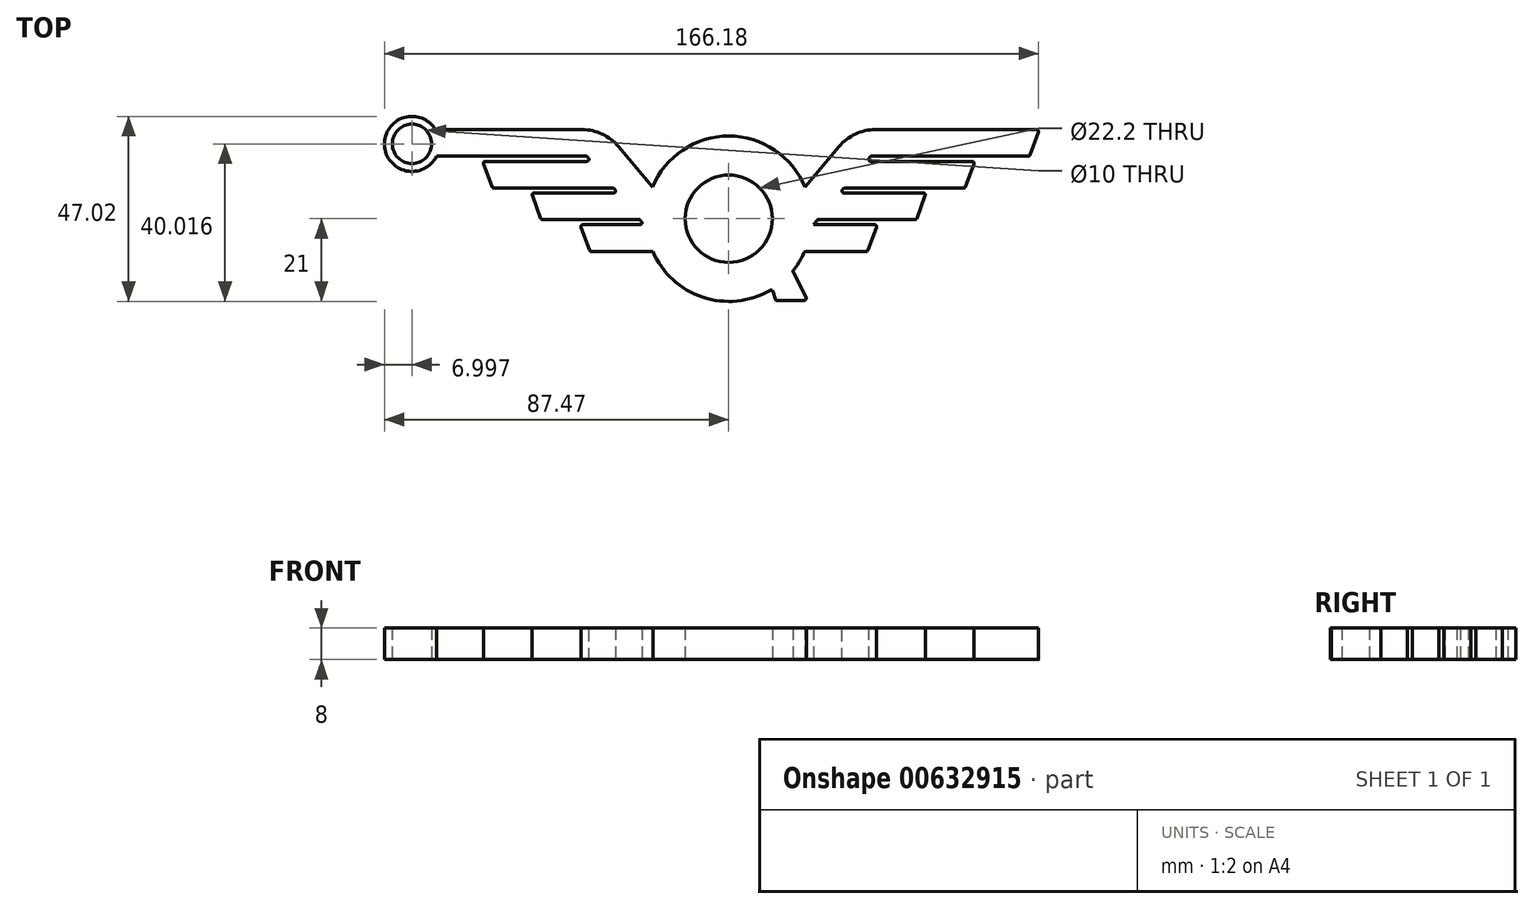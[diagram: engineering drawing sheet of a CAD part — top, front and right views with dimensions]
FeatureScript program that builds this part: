
annotation { "Feature Type Name" : "Feature", "Feature Type Description" : "" }
export const myFeature = defineFeature(function(context is Context, id is Id, definition is map)
    precondition{}
    {
        {
            var Q0;
            Q0=qCreatedBy(makeId("Top.planeOp"),FACE);
            var sketch = newSketch(context, id + "F0", { "sketchPlane" : qUnion([Q0])});
            skCircle(sketch, "E0", {"center": v(0, 0) * mm, "radius": 21 * mm});
            skLineSegment(sketch, "E1", {"start": v(11, -17.89) * mm, "end": v(12, -20.84) * mm});
            skLineSegment(sketch, "E2", {"start": v(12, -20.84) * mm, "end": v(20, -20.74) * mm});
            skLineSegment(sketch, "E3", {"start": v(20, -20.74) * mm, "end": v(16.26, -13.29) * mm});
            skCircle(sketch, "E4.0", {"center": v(0, 0) * mm, "radius": 11.1 * mm});
            skLineSegment(sketch, "E5", {"start": v(37.76, -1.52) * mm, "end": v(20.94, -1.52) * mm});
            skLineSegment(sketch, "E6", {"start": v(35.3, -8.29) * mm, "end": v(19.3, -8.29) * mm});
            skLineSegment(sketch, "E7", {"start": v(37.76, -1.52) * mm, "end": v(35.3, -8.29) * mm});
            skLineSegment(sketch, "E8.MirrorCS", {"start": v(-37.76, -1.52) * mm, "end": v(-20.94, -1.52) * mm});
            skLineSegment(sketch, "E9.MirrorCS", {"start": v(-35.3, -8.29) * mm, "end": v(-19.3, -8.29) * mm});
            skLineSegment(sketch, "E10.MirrorCS", {"start": v(-37.76, -1.52) * mm, "end": v(-35.3, -8.29) * mm});
            skLineSegment(sketch, "E11", {"start": v(31.64, 22.63) * mm, "end": v(78.92, 22.63) * mm});
            skLineSegment(sketch, "E12", {"start": v(54.5, 15.87) * mm, "end": v(62.74, 15.87) * mm});
            skLineSegment(sketch, "E13", {"start": v(78.92, 22.63) * mm, "end": v(76.46, 15.87) * mm});
            skLineSegment(sketch, "E14", {"start": v(76.46, 15.87) * mm, "end": v(62.74, 15.87) * mm});
            skLineSegment(sketch, "E15", {"start": v(54.5, 15.87) * mm, "end": v(36.02, 15.87) * mm});
            skLineSegment(sketch, "E16", {"start": v(47.43, 7.82) * mm, "end": v(60.05, 7.82) * mm});
            skLineSegment(sketch, "E17", {"start": v(62.52, 14.59) * mm, "end": v(60.05, 7.82) * mm});
            skLineSegment(sketch, "E18", {"start": v(29.64, 6.54) * mm, "end": v(50.14, 6.54) * mm});
            skLineSegment(sketch, "E19", {"start": v(23, -0.22) * mm, "end": v(47.67, -0.22) * mm});
            skLineSegment(sketch, "E20", {"start": v(50.14, 6.54) * mm, "end": v(47.67, -0.22) * mm});
            skLineSegment(sketch, "E21", {"start": v(34.95, 14.59) * mm, "end": v(43.97, 14.59) * mm});
            skLineSegment(sketch, "E22", {"start": v(47.43, 7.82) * mm, "end": v(29.29, 7.82) * mm});
            skLineSegment(sketch, "E23", {"start": v(47.67, -0.22) * mm, "end": v(22.55, -0.22) * mm});
            skLineSegment(sketch, "E24", {"start": v(22.55, -0.22) * mm, "end": v(21.47, -1.52) * mm});
            skLineSegment(sketch, "E25", {"start": v(62.52, 14.59) * mm, "end": v(34.95, 14.59) * mm});
            skLineSegment(sketch, "E26", {"start": v(36.02, 15.87) * mm, "end": v(34.95, 14.59) * mm});
            skLineSegment(sketch, "E27", {"start": v(43.97, 14.59) * mm, "end": v(34.95, 14.59) * mm});
            skLineSegment(sketch, "E28", {"start": v(29.64, 6.54) * mm, "end": v(28.21, 6.54) * mm});
            skLineSegment(sketch, "E29", {"start": v(29.29, 7.82) * mm, "end": v(28.21, 6.54) * mm});
            skLineSegment(sketch, "E30", {"start": v(31.64, 22.63) * mm, "end": v(19.4, 8.02) * mm});
            skLineSegment(sketch, "E31.MirrorCS", {"start": v(-31.64, 22.63) * mm, "end": v(-19.4, 8.02) * mm});
            skLineSegment(sketch, "E32.MirrorCS", {"start": v(-31.64, 22.63) * mm, "end": v(-78.92, 22.63) * mm});
            skLineSegment(sketch, "E33.MirrorCS", {"start": v(-54.5, 15.87) * mm, "end": v(-36.02, 15.87) * mm});
            skLineSegment(sketch, "E34.MirrorCS", {"start": v(-34.95, 14.59) * mm, "end": v(-43.97, 14.59) * mm});
            skLineSegment(sketch, "E35.MirrorCS", {"start": v(-36.02, 15.87) * mm, "end": v(-34.95, 14.59) * mm});
            skLineSegment(sketch, "E36.MirrorCS", {"start": v(-54.5, 15.87) * mm, "end": v(-62.74, 15.87) * mm});
            skLineSegment(sketch, "E37.MirrorCS", {"start": v(-76.46, 15.87) * mm, "end": v(-62.74, 15.87) * mm});
            skLineSegment(sketch, "E38.MirrorCS", {"start": v(-78.92, 22.63) * mm, "end": v(-76.46, 15.87) * mm});
            skLineSegment(sketch, "E39.MirrorCS", {"start": v(-62.52, 14.59) * mm, "end": v(-34.95, 14.59) * mm});
            skLineSegment(sketch, "E40.MirrorCS", {"start": v(-62.52, 14.59) * mm, "end": v(-60.05, 7.82) * mm});
            skLineSegment(sketch, "E41.MirrorCS", {"start": v(-47.43, 7.82) * mm, "end": v(-60.05, 7.82) * mm});
            skLineSegment(sketch, "E42.MirrorCS", {"start": v(-47.43, 7.82) * mm, "end": v(-29.29, 7.82) * mm});
            skLineSegment(sketch, "E43.MirrorCS", {"start": v(-29.29, 7.82) * mm, "end": v(-28.21, 6.54) * mm});
            skLineSegment(sketch, "E44.MirrorCS", {"start": v(-29.64, 6.54) * mm, "end": v(-28.21, 6.54) * mm});
            skLineSegment(sketch, "E45.MirrorCS", {"start": v(-29.64, 6.54) * mm, "end": v(-50.14, 6.54) * mm});
            skLineSegment(sketch, "E46.MirrorCS", {"start": v(-50.14, 6.54) * mm, "end": v(-47.67, -0.22) * mm});
            skLineSegment(sketch, "E47.MirrorCS", {"start": v(-47.67, -0.22) * mm, "end": v(-22.55, -0.22) * mm});
            skLineSegment(sketch, "E48.MirrorCS", {"start": v(-22.55, -0.22) * mm, "end": v(-21.47, -1.52) * mm});
            skSolve(sketch);
        }
        {
            var Q0;
            Q0=makeQuery(id+"F0.imprint","IMPRINT",FACE,{"disambiguationData":[TD([[makeQuery(id+"F0.imprint","IMPRINT",EDGE,{"derivedFrom":sQuery(id+"F0.wireOp",EDGE,"E4.0")}),-1.0]])]});
            var Q1;
            {var subQ0=sQuery(id+"F0.wireOp",EDGE,"E1");Q1=makeQuery(id+"F0.imprint","IMPRINT",FACE,{"disambiguationData":[TD([[makeQuery(id+"F0.imprint","IMPRINT",EDGE,{"derivedFrom":subQ0}),1.0]])]});}
            extrude(context, id + "F1", {"entities" : qUnion([Q0, Q1]), "endBound" : BoundingType.SYMMETRIC, "depth" : 8 * mm, "offsetDistance" : 25 * mm});
        }
        {
            var Q0;
            {var subQ3=sQuery(id+"F0.wireOp",EDGE,"dh19a1xa-YlTx-h9a7-XIYp-d6YBFNoYxual");Q0=makeQuery(id+"F0.imprint","IMPRINT",FACE,{"disambiguationData":[TD([[makeQuery(id+"F0.imprint","IMPRINT",EDGE,{"derivedFrom":subQ3}),-1.0]])]});}
            var Q1;
            {var subQ0=sQuery(id+"F0.wireOp",EDGE,"E6");Q1=makeQuery(id+"F0.imprint","IMPRINT",FACE,{"disambiguationData":[TD([[makeQuery(id+"F0.imprint","IMPRINT",EDGE,{"derivedFrom":subQ0}),-1.0]])]});}
            extrude(context, id + "F2", {"entities" : qUnion([Q0, Q1]), "operationType" : NewBodyOperationType.ADD, "endBound" : BoundingType.SYMMETRIC, "depth" : 8 * mm, "offsetDistance" : 25 * mm});
        }
        {
            var Q0;
            Q0=makeQuery(id+"F0.imprint","IMPRINT",FACE,{"disambiguationData":[TD([[makeQuery(id+"F0.imprint","IMPRINT",EDGE,{"derivedFrom":sQuery(id+"F0.wireOp",EDGE,"E11")}),-1.0]])]});
            extrude(context, id + "F3", {"entities" : qUnion([Q0]), "operationType" : NewBodyOperationType.ADD, "endBound" : BoundingType.SYMMETRIC, "depth" : 8 * mm, "offsetDistance" : 25 * mm});
        }
        {
            var Q0;
            Q0 = qSketchRegion(id + "F0", true);
            extrude(context, id + "F4", {"entities" : qUnion([Q0]), "operationType" : NewBodyOperationType.ADD, "endBound" : BoundingType.SYMMETRIC, "depth" : 8 * mm, "offsetDistance" : 25 * mm});
        }
        {
            var Q0;
            Q0=makeQuery(id+"F4.opExtrude","SWEPT_EDGE",EDGE,{"disambiguationData":[OSD([sQuery(id+"F0.wireOp",EDGE,"E33.MirrorCS"),sQuery(id+"F0.wireOp",EDGE,"E35.MirrorCS")])]});
            var Q1;
            Q1=makeQuery(id+"F4.opExtrude","SWEPT_EDGE",EDGE,{"disambiguationData":[OSD([sQuery(id+"F0.wireOp",EDGE,"E42.MirrorCS"),sQuery(id+"F0.wireOp",EDGE,"E43.MirrorCS")])]});
            var Q2;
            Q2=makeQuery(id+"F4.opExtrude","SWEPT_EDGE",EDGE,{"disambiguationData":[OSD([sQuery(id+"F0.wireOp",EDGE,"E48.MirrorCS"),sQuery(id+"F0.wireOp",EDGE,"E47.MirrorCS")])]});
            var Q3;
            Q3=makeQuery(id+"F4.opExtrude","SWEPT_EDGE",EDGE,{"disambiguationData":[OSD([sQuery(id+"F0.wireOp",EDGE,"E0"),sQuery(id+"F0.wireOp",EDGE,"E9.MirrorCS")])]});
            var Q4;
            Q4=makeQuery(id+"F4.opExtrude","SWEPT_EDGE",EDGE,{"disambiguationData":[OSD([sQuery(id+"F0.wireOp",EDGE,"E8.MirrorCS"),sQuery(id+"F0.wireOp",EDGE,"E48.MirrorCS")])]});
            var Q5;
            Q5=makeQuery(id+"F4.opExtrude","SWEPT_EDGE",EDGE,{"disambiguationData":[OSD([sQuery(id+"F0.wireOp",EDGE,"E43.MirrorCS"),sQuery(id+"F0.wireOp",EDGE,"E44.MirrorCS")])]});
            var Q6;
            Q6=makeQuery(id+"F4.opExtrude","SWEPT_EDGE",EDGE,{"disambiguationData":[OSD([sQuery(id+"F0.wireOp",EDGE,"E35.MirrorCS"),sQuery(id+"F0.wireOp",EDGE,"E39.MirrorCS")])]});
            var Q7;
            Q7=makeQuery(id+"F4.opExtrude","SWEPT_EDGE",EDGE,{"disambiguationData":[OSD([sQuery(id+"F0.wireOp",EDGE,"E32.MirrorCS"),sQuery(id+"F0.wireOp",EDGE,"E38.MirrorCS")])]});
            var Q8;
            Q8=makeQuery(id+"F4.opExtrude","SWEPT_EDGE",EDGE,{"disambiguationData":[OSD([sQuery(id+"F0.wireOp",EDGE,"E37.MirrorCS"),sQuery(id+"F0.wireOp",EDGE,"E38.MirrorCS")])]});
            var Q9;
            Q9=makeQuery(id+"F4.opExtrude","SWEPT_EDGE",EDGE,{"disambiguationData":[OSD([sQuery(id+"F0.wireOp",EDGE,"E39.MirrorCS"),sQuery(id+"F0.wireOp",EDGE,"E40.MirrorCS")])]});
            var Q10;
            Q10=makeQuery(id+"F4.opExtrude","SWEPT_EDGE",EDGE,{"disambiguationData":[OSD([sQuery(id+"F0.wireOp",EDGE,"E40.MirrorCS"),sQuery(id+"F0.wireOp",EDGE,"E41.MirrorCS")])]});
            var Q11;
            Q11=makeQuery(id+"F4.opExtrude","SWEPT_EDGE",EDGE,{"disambiguationData":[OSD([sQuery(id+"F0.wireOp",EDGE,"E45.MirrorCS"),sQuery(id+"F0.wireOp",EDGE,"E46.MirrorCS")])]});
            var Q12;
            Q12=makeQuery(id+"F4.opExtrude","SWEPT_EDGE",EDGE,{"disambiguationData":[OSD([sQuery(id+"F0.wireOp",EDGE,"E8.MirrorCS"),sQuery(id+"F0.wireOp",EDGE,"E10.MirrorCS")])]});
            var Q13;
            Q13=makeQuery(id+"F4.opExtrude","SWEPT_EDGE",EDGE,{"disambiguationData":[OSD([sQuery(id+"F0.wireOp",EDGE,"E9.MirrorCS"),sQuery(id+"F0.wireOp",EDGE,"E10.MirrorCS")])]});
            var Q14;
            Q14=makeQuery(id+"F4.opExtrude","SWEPT_EDGE",EDGE,{"disambiguationData":[OSD([sQuery(id+"F0.wireOp",EDGE,"E46.MirrorCS"),sQuery(id+"F0.wireOp",EDGE,"E47.MirrorCS")])]});
            var Q15;
            Q15=makeQuery(id+"F3.opExtrude","SWEPT_EDGE",EDGE,{"disambiguationData":[OSD([sQuery(id+"F0.wireOp",EDGE,"E11"),sQuery(id+"F0.wireOp",EDGE,"E13")])]});
            var Q16;
            Q16=makeQuery(id+"F3.opExtrude","SWEPT_EDGE",EDGE,{"disambiguationData":[OSD([sQuery(id+"F0.wireOp",EDGE,"E13"),sQuery(id+"F0.wireOp",EDGE,"E14")])]});
            var Q17;
            Q17=makeQuery(id+"F3.opExtrude","SWEPT_EDGE",EDGE,{"disambiguationData":[OSD([sQuery(id+"F0.wireOp",EDGE,"E17"),sQuery(id+"F0.wireOp",EDGE,"E25")])]});
            var Q18;
            Q18=makeQuery(id+"F3.opExtrude","SWEPT_EDGE",EDGE,{"disambiguationData":[OSD([sQuery(id+"F0.wireOp",EDGE,"E16"),sQuery(id+"F0.wireOp",EDGE,"E17")])]});
            var Q19;
            Q19=makeQuery(id+"F3.opExtrude","SWEPT_EDGE",EDGE,{"disambiguationData":[OSD([sQuery(id+"F0.wireOp",EDGE,"E18"),sQuery(id+"F0.wireOp",EDGE,"E20")])]});
            var Q20;
            Q20=makeQuery(id+"F2.opExtrude","SWEPT_EDGE",EDGE,{"disambiguationData":[OSD([sQuery(id+"F0.wireOp",EDGE,"E5"),sQuery(id+"F0.wireOp",EDGE,"E7")])]});
            var Q21;
            Q21=makeQuery(id+"F2.opExtrude","SWEPT_EDGE",EDGE,{"disambiguationData":[OSD([sQuery(id+"F0.wireOp",EDGE,"E6"),sQuery(id+"F0.wireOp",EDGE,"E7")])]});
            var Q22;
            Q22=makeQuery(id+"F3.opExtrude","SWEPT_EDGE",EDGE,{"disambiguationData":[OSD([sQuery(id+"F0.wireOp",EDGE,"E20"),sQuery(id+"F0.wireOp",EDGE,"E23")])]});
            var Q23;
            Q23=makeQuery(id+"F3.opExtrude","SWEPT_EDGE",EDGE,{"disambiguationData":[OSD([sQuery(id+"F0.wireOp",EDGE,"E5"),sQuery(id+"F0.wireOp",EDGE,"E24")])]});
            var Q24;
            Q24=makeQuery(id+"F3.opExtrude","SWEPT_EDGE",EDGE,{"disambiguationData":[OSD([sQuery(id+"F0.wireOp",EDGE,"E28"),sQuery(id+"F0.wireOp",EDGE,"E29")])]});
            var Q25;
            Q25=makeQuery(id+"F3.opExtrude","SWEPT_EDGE",EDGE,{"disambiguationData":[OSD([sQuery(id+"F0.wireOp",EDGE,"E26"),sQuery(id+"F0.wireOp",EDGE,"E27")])]});
            var Q26;
            Q26=makeQuery(id+"F3.opExtrude","SWEPT_EDGE",EDGE,{"disambiguationData":[OSD([sQuery(id+"F0.wireOp",EDGE,"E15"),sQuery(id+"F0.wireOp",EDGE,"E26")])]});
            var Q27;
            Q27=makeQuery(id+"F3.opExtrude","SWEPT_EDGE",EDGE,{"disambiguationData":[OSD([sQuery(id+"F0.wireOp",EDGE,"E22"),sQuery(id+"F0.wireOp",EDGE,"E29")])]});
            var Q28;
            Q28=makeQuery(id+"F3.opExtrude","SWEPT_EDGE",EDGE,{"disambiguationData":[OSD([sQuery(id+"F0.wireOp",EDGE,"E23"),sQuery(id+"F0.wireOp",EDGE,"E24")])]});
            var Q29;
            Q29=makeQuery(id+"F2.opExtrude","SWEPT_EDGE",EDGE,{"disambiguationData":[OSD([sQuery(id+"F0.wireOp",EDGE,"E0"),sQuery(id+"F0.wireOp",EDGE,"E6")])]});
            var Q30;
            Q30=makeQuery(id+"F1.opExtrude","SWEPT_EDGE",EDGE,{"disambiguationData":[OSD([sQuery(id+"F0.wireOp",EDGE,"E2"),sQuery(id+"F0.wireOp",EDGE,"E3")])]});
            var Q31;
            Q31=makeQuery(id+"F1.opExtrude","SWEPT_EDGE",EDGE,{"disambiguationData":[OSD([sQuery(id+"F0.wireOp",EDGE,"E1"),sQuery(id+"F0.wireOp",EDGE,"E2")])]});
            var Q32;
            Q32=makeQuery(id+"F1.opExtrude","SWEPT_EDGE",EDGE,{"disambiguationData":[OSD([sQuery(id+"F0.wireOp",EDGE,"E0"),sQuery(id+"F0.wireOp",EDGE,"E1")])]});
            var Q33;
            Q33=makeQuery(id+"F1.opExtrude","SWEPT_EDGE",EDGE,{"disambiguationData":[OSD([sQuery(id+"F0.wireOp",EDGE,"E0"),sQuery(id+"F0.wireOp",EDGE,"E3")])]});
            fillet(context, id + "F5", {"entities" : qUnion([Q0, Q1, Q2, Q3, Q4, Q5, Q6, Q7, Q8, Q9, Q10, Q11, Q12, Q13, Q14, Q15, Q16, Q17, Q18, Q19, Q20, Q21, Q22, Q23, Q24, Q25, Q26, Q27, Q28, Q29, Q30, Q31, Q32, Q33]), "radius" : .5 * mm, "tangentPropagation" : true, "allowEdgeOverflow" : false});
        }
        {
            var Q0;
            Q0=qCreatedBy(makeId("Top.planeOp"),FACE);
            var sketch = newSketch(context, id + "F6", { "sketchPlane" : qUnion([Q0])});
            skCircle(sketch, "E49", {"center": v(-80.47, 19.02) * mm, "radius": 7 * mm});
            skCircle(sketch, "E50.0", {"center": v(-80.47, 19.02) * mm, "radius": 5 * mm});
            skSolve(sketch);
        }
        {
            var Q0;
            Q0 = qSketchRegion(id + "F6", true);
            extrude(context, id + "F7", {"entities" : qUnion([Q0]), "operationType" : NewBodyOperationType.ADD, "endBound" : BoundingType.SYMMETRIC, "depth" : 8 * mm, "offsetDistance" : 25 * mm});
        }
        {
            var Q0;
            {var subQ0=sQuery(id+"F0.wireOp",EDGE,"E30");var subQ1=sQuery(id+"F0.wireOp",EDGE,"E29");var subQ2=sQuery(id+"F0.wireOp",EDGE,"E28");var subQ3=sQuery(id+"F0.wireOp",EDGE,"E27");var subQ4=sQuery(id+"F0.wireOp",EDGE,"E26");var subQ5=sQuery(id+"F0.wireOp",EDGE,"E25");var subQ6=sQuery(id+"F0.wireOp",EDGE,"E24");var subQ7=sQuery(id+"F0.wireOp",EDGE,"E23");var subQ8=sQuery(id+"F0.wireOp",EDGE,"E22");var subQ9=sQuery(id+"F0.wireOp",EDGE,"E15");var subQ10=sQuery(id+"F0.wireOp",EDGE,"E20");var subQ11=sQuery(id+"F0.wireOp",EDGE,"E18");var subQ12=sQuery(id+"F0.wireOp",EDGE,"E17");var subQ13=sQuery(id+"F0.wireOp",EDGE,"E16");var subQ14=sQuery(id+"F0.wireOp",EDGE,"E14");var subQ15=sQuery(id+"F0.wireOp",EDGE,"E13");var subQ16=sQuery(id+"F0.wireOp",EDGE,"E12");var subQ17=sQuery(id+"F0.wireOp",EDGE,"E11");var subQ18=sQuery(id+"F0.wireOp",EDGE,"E7");var subQ19=sQuery(id+"F0.wireOp",EDGE,"E6");var subQ20=sQuery(id+"F0.wireOp",EDGE,"E5");var subQ21=sQuery(id+"F0.wireOp",EDGE,"E4.0");var subQ22=sQuery(id+"F0.wireOp",EDGE,"E3");var subQ23=sQuery(id+"F0.wireOp",EDGE,"E2");var subQ24=sQuery(id+"F0.wireOp",EDGE,"E1");var subQ25=sQuery(id+"F0.wireOp",EDGE,"E0");Q0=makeQuery(id+"F7.boolean.opBoolean","MERGE",FACE,{"derivedFrom":[makeQuery(id+"F4.boolean.opBoolean","MERGE",FACE,{"derivedFrom":[makeQuery(id+"F3.boolean.opBoolean","MERGE",FACE,{"derivedFrom":[makeQuery(id+"F2.boolean.opBoolean","MERGE",FACE,{"derivedFrom":[makeQuery(id+"F1.opExtrude","CAP_FACE",FACE,{"disambiguationData":[OSD([subQ25,subQ24,subQ23,subQ22,subQ21])],"isStart":false}),makeQuery(id+"F2.opExtrude","CAP_FACE",FACE,{"disambiguationData":[OSD([subQ25,subQ20,subQ19,subQ18])],"isStart":false})]}),makeQuery(id+"F3.opExtrude","CAP_FACE",FACE,{"disambiguationData":[OSD([subQ25,subQ20,subQ17,subQ16,subQ15,subQ14,subQ13,subQ12,subQ11,subQ10,subQ9,subQ8,subQ7,subQ6,subQ5,subQ4,subQ3,subQ2,subQ1,subQ0])],"isStart":false})]}),makeQuery(id+"F4.opExtrude","CAP_FACE",FACE,{"disambiguationData":[OSD([subQ25,subQ24,subQ23,subQ22,subQ21,subQ20,subQ19,subQ18,sQuery(id+"F0.wireOp",EDGE,"E8.MirrorCS"),sQuery(id+"F0.wireOp",EDGE,"E9.MirrorCS"),sQuery(id+"F0.wireOp",EDGE,"E10.MirrorCS"),subQ17,subQ16,subQ15,subQ14,subQ13,subQ12,subQ11,subQ10,subQ9,subQ8,subQ7,subQ6,subQ5,subQ4,subQ3,subQ2,subQ1,subQ0,sQuery(id+"F0.wireOp",EDGE,"E31.MirrorCS"),sQuery(id+"F0.wireOp",EDGE,"E32.MirrorCS"),sQuery(id+"F0.wireOp",EDGE,"E33.MirrorCS"),sQuery(id+"F0.wireOp",EDGE,"E35.MirrorCS"),sQuery(id+"F0.wireOp",EDGE,"E36.MirrorCS"),sQuery(id+"F0.wireOp",EDGE,"E37.MirrorCS"),sQuery(id+"F0.wireOp",EDGE,"E38.MirrorCS"),sQuery(id+"F0.wireOp",EDGE,"E39.MirrorCS"),sQuery(id+"F0.wireOp",EDGE,"E40.MirrorCS"),sQuery(id+"F0.wireOp",EDGE,"E41.MirrorCS"),sQuery(id+"F0.wireOp",EDGE,"E42.MirrorCS"),sQuery(id+"F0.wireOp",EDGE,"E43.MirrorCS"),sQuery(id+"F0.wireOp",EDGE,"E44.MirrorCS"),sQuery(id+"F0.wireOp",EDGE,"E45.MirrorCS"),sQuery(id+"F0.wireOp",EDGE,"E46.MirrorCS"),sQuery(id+"F0.wireOp",EDGE,"E48.MirrorCS"),sQuery(id+"F0.wireOp",EDGE,"E47.MirrorCS")])],"isStart":false})]}),makeQuery(id+"F7.opExtrude","CAP_FACE",FACE,{"disambiguationData":[OSD([sQuery(id+"F6.wireOp",EDGE,"E49"),sQuery(id+"F6.wireOp",EDGE,"E50.0")])],"isStart":false})]});}
            var sketch = newSketch(context, id + "F8", { "sketchPlane" : qUnion([Q0])});
            skCircle(sketch, "E51", {"center": v(-80.47, 19.02) * mm, "radius": 5 * mm});
            skSolve(sketch);
        }
        {
            var Q0;
            Q0 = qSketchRegion(id + "F8", true);
            extrude(context, id + "F9", {"entities" : qUnion([Q0]), "operationType" : NewBodyOperationType.REMOVE, "oppositeDirection" : true, "depth" : 25 * mm, "offsetDistance" : 25 * mm});
        }
        {
            var Q0;
            Q0=makeQuery(id+"F4.opExtrude","SWEPT_EDGE",EDGE,{"disambiguationData":[OSD([sQuery(id+"F0.wireOp",EDGE,"E31.MirrorCS"),sQuery(id+"F0.wireOp",EDGE,"E32.MirrorCS")])]});
            var Q1;
            Q1=makeQuery(id+"F3.opExtrude","SWEPT_EDGE",EDGE,{"disambiguationData":[OSD([sQuery(id+"F0.wireOp",EDGE,"E11"),sQuery(id+"F0.wireOp",EDGE,"E30")])]});
            fillet(context, id + "F10", {"entities" : qUnion([Q0, Q1]), "radius" : 12 * mm, "tangentPropagation" : true, "allowEdgeOverflow" : false});
        }
    });
